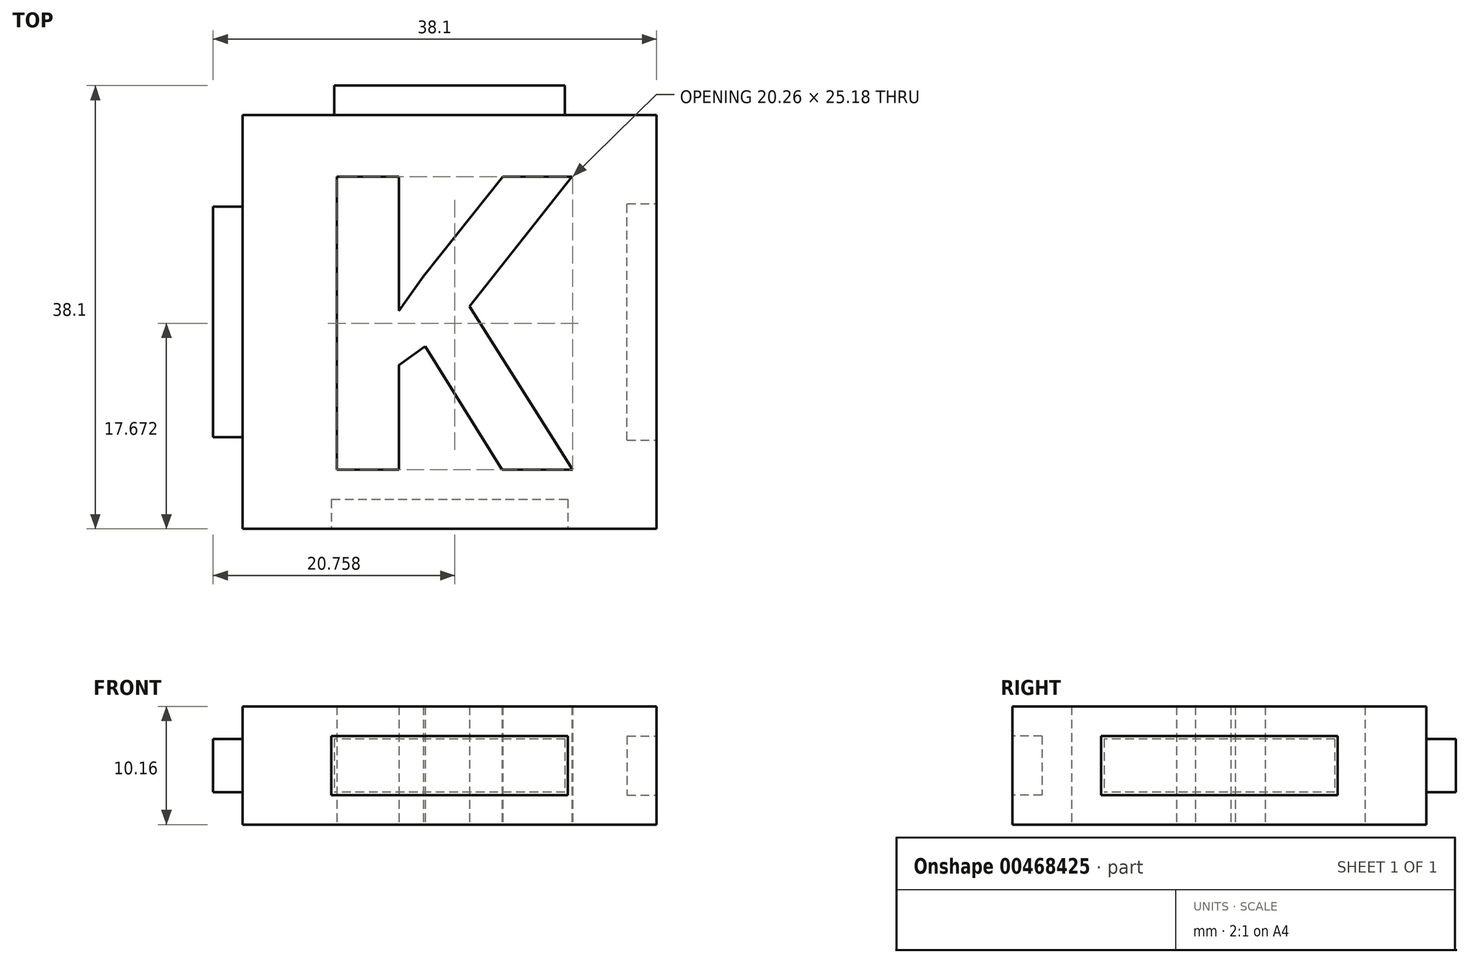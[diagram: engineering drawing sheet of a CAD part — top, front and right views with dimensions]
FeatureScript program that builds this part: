
annotation { "Feature Type Name" : "Feature", "Feature Type Description" : "" }
export const myFeature = defineFeature(function(context is Context, id is Id, definition is map)
    precondition{}
    {
        {
            var Q0;
            Q0=qCreatedBy(makeId("Top.planeOp"),FACE);
            var sketch = newSketch(context, id + "F0", { "sketchPlane" : qUnion([Q0])});
            skLineSegment(sketch, "E0.bottom", {"start": v(-17.78, 17.78) * mm, "end": v(17.78, 17.78) * mm});
            skLineSegment(sketch, "E0.top", {"start": v(-17.78, -17.78) * mm, "end": v(17.78, -17.78) * mm});
            skLineSegment(sketch, "E0.left", {"start": v(-17.78, 17.78) * mm, "end": v(-17.78, -17.78) * mm});
            skLineSegment(sketch, "E0.right", {"start": v(17.78, 17.78) * mm, "end": v(17.78, -17.78) * mm});
            skText(sketch, "E1", { "text": "K", "fontName": "OpenSans-Bold.ttf"});
            const initialGuessF0  = {"E1": [-0.01286, -0.0127, 1, 0, 0.0254]};
            skSetInitialGuess(sketch, initialGuessF0);
            skSolve(sketch);
        }
        {
            var Q0;
            Q0=qSketchRegion(id+"F0",true);
            extrude(context, id + "F1", {"entities" : qUnion([Q0]), "endBound" : BoundingType.SYMMETRIC, "depth" : 10.16 * mm});
        }
        {
            var Q0;
            Q0=makeQuery(id+"F1.opExtrude","SWEPT_FACE",FACE,{"disambiguationData":[OSD([sQuery(id+"F0.wireOp",EDGE,"E0.bottom")])]});
            var sketch = newSketch(context, id + "F2", { "sketchPlane" : qUnion([Q0])});
            skLineSegment(sketch, "E2.bottom", {"start": v(-9.9, 2.29) * mm, "end": v(9.9, 2.29) * mm});
            skLineSegment(sketch, "E2.top", {"start": v(-9.9, -2.29) * mm, "end": v(9.9, -2.29) * mm});
            skLineSegment(sketch, "E2.left", {"start": v(-9.9, 2.29) * mm, "end": v(-9.9, -2.29) * mm});
            skLineSegment(sketch, "E2.right", {"start": v(9.9, 2.29) * mm, "end": v(9.9, -2.29) * mm});
            skSolve(sketch);
        }
        {
            var Q0;
            Q0=qSketchRegion(id+"F2",true);
            extrude(context, id + "F3", {"entities" : qUnion([Q0]), "operationType" : NewBodyOperationType.ADD, "depth" : 2.54 * mm});
        }
        {
            var Q0;
            Q0=makeQuery(id+"F1.opExtrude","SWEPT_FACE",FACE,{"disambiguationData":[OSD([sQuery(id+"F0.wireOp",EDGE,"E0.left")])]});
            var sketch = newSketch(context, id + "F4", { "sketchPlane" : qUnion([Q0])});
            skLineSegment(sketch, "E3.bottom", {"start": v(-9.9, 2.29) * mm, "end": v(9.9, 2.29) * mm});
            skLineSegment(sketch, "E3.top", {"start": v(-9.9, -2.29) * mm, "end": v(9.9, -2.29) * mm});
            skLineSegment(sketch, "E3.left", {"start": v(-9.9, 2.29) * mm, "end": v(-9.9, -2.29) * mm});
            skLineSegment(sketch, "E3.right", {"start": v(9.9, 2.29) * mm, "end": v(9.9, -2.29) * mm});
            skSolve(sketch);
        }
        {
            var Q0;
            Q0=qSketchRegion(id+"F4",true);
            extrude(context, id + "F5", {"entities" : qUnion([Q0]), "operationType" : NewBodyOperationType.ADD, "depth" : 2.54 * mm});
        }
        {
            var Q0;
            Q0=makeQuery(id+"F1.opExtrude","SWEPT_FACE",FACE,{"disambiguationData":[OSD([sQuery(id+"F0.wireOp",EDGE,"E0.top")])]});
            var sketch = newSketch(context, id + "F6", { "sketchPlane" : qUnion([Q0])});
            skLineSegment(sketch, "E4.bottom", {"start": v(-10.16, 2.54) * mm, "end": v(10.16, 2.54) * mm});
            skLineSegment(sketch, "E4.top", {"start": v(-10.16, -2.54) * mm, "end": v(10.16, -2.54) * mm});
            skLineSegment(sketch, "E4.left", {"start": v(-10.16, 2.54) * mm, "end": v(-10.16, -2.54) * mm});
            skLineSegment(sketch, "E4.right", {"start": v(10.16, 2.54) * mm, "end": v(10.16, -2.54) * mm});
            skSolve(sketch);
        }
        {
            var Q0;
            Q0=qSketchRegion(id+"F6",true);
            extrude(context, id + "F7", {"entities" : qUnion([Q0]), "operationType" : NewBodyOperationType.REMOVE, "oppositeDirection" : true, "depth" : 2.54 * mm});
        }
        {
            var Q0;
            Q0=makeQuery(id+"F1.opExtrude","SWEPT_FACE",FACE,{"disambiguationData":[OSD([sQuery(id+"F0.wireOp",EDGE,"E0.right")])]});
            var sketch = newSketch(context, id + "F8", { "sketchPlane" : qUnion([Q0])});
            skLineSegment(sketch, "E5.bottom", {"start": v(-10.16, 2.54) * mm, "end": v(10.16, 2.54) * mm});
            skLineSegment(sketch, "E5.top", {"start": v(-10.16, -2.54) * mm, "end": v(10.16, -2.54) * mm});
            skLineSegment(sketch, "E5.left", {"start": v(-10.16, 2.54) * mm, "end": v(-10.16, -2.54) * mm});
            skLineSegment(sketch, "E5.right", {"start": v(10.16, 2.54) * mm, "end": v(10.16, -2.54) * mm});
            skSolve(sketch);
        }
        {
            var Q0;
            Q0=qSketchRegion(id+"F8",true);
            extrude(context, id + "F9", {"entities" : qUnion([Q0]), "operationType" : NewBodyOperationType.REMOVE, "oppositeDirection" : true, "depth" : 2.54 * mm});
        }
    });
